# Revit family: P200635WX-009c_WED6620H_CW
name_source: partatom
category: Specialty Equipment
units: mm (PartAtom-declared; Revit-internal decimal feet)

## family parameters
Always vertical = Yes
Cut with Voids When Loaded = No
Enable Cutting in Views = No
Maintain Annotation Orientation = No
Part Type = Normal
Room Calculation Point = No
Round Connector Dimension = Use Diameter
Shared = No
Work Plane-Based = No

## types (2) — shared parameters
Accent Material = ARCAT - Plastic - Gray
Amps = 0 A
Back Panel Material = ARCAT - Metal - Aluminum
Clearance Material = ARCAT - Clearance
Default Elevation = 0"
Depth = 31"
Description = 7.4 cu. ft. Front Load Electric Dryer with Steam Cycles
Sécheuse électrique avec programmes assistés à la vapeur, 7.4 pi³
Display Material = ARCAT - Plastic - Black
Dsiplay Panel Material = ARCAT - Glass Tempered - Black
Family Name = Electric Front-Load Dryer
Feature 1 = Wrinkle Shield™ Plus Option with Steam
Programme de rafraîchissement à la vapeur
Feature 2 = 7.4 cu. ft. Capacity
Option de prévention des faux plis Wrinkle Shield™ Plus avec vapeur
Feature 3 = ENERGY STAR® Certified
Capacité de 7,4 pi³
Glass Material = ARCAT - Glass Tempered - Clear
Height = 38 3/4"
Installation-Fabrication = https://www.whirlpool.com
https://www.whirlpool.com
Manufacturer = Whirlpool
Voltage = 0 V
Width = 27"

## per-type parameters (varying)
| type | Body Material | Button Panal Material | Chrome Trim Material | Door Material | Door Panel Material | Leg Material |
| WED6620HC | ARCAT - Metal - Gray | ARCAT - Plastic - Dark Grey | ARCAT - Metal - Chrome | ARCAT - Metal - Gray | ARCAT - Metal - Gray | <By Category> |
| WED6620HW | ARCAT - Metal - White | ARCAT - Plastic - White | ARCAT - Metal - Chrome Black | ARCAT - Metal - White | ARCAT - Metal - Steel - Black - Light | ARCAT - Plastic - White |

note: column(s) folded — value = type name in every type: Model

## geometry (parser evidence)
native form markers: Sweep x4
no freeform markers — native parametric forms only
